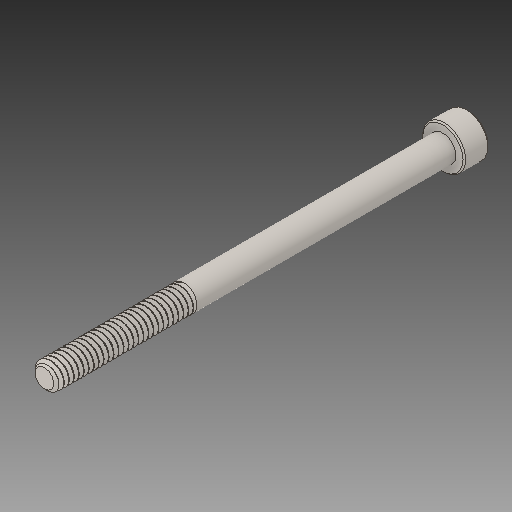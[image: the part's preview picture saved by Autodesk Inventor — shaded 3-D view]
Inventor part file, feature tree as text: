
AUTODESK INVENTOR PART (.ipt)
format: ipt  version: 2017 (Build 210142000, 142)  size: 690,688 bytes
history: native  units: in
note: dims shown in document units (in); Inventor stores cm internally (conversion verified against a paired STEP export)
features: chamfer x1
ambient origin geometry x8: Origin, YZ Plane, XZ Plane, XY Plane, X Axis, Y Axis, Z Axis, Center Point
bodies: Solid1 (feature_tree)
feature tree (1):
  chamfer  "Chamfer2"  [1 undecoded]
note: 1 required parameter value undecoded (feature->parameter linkage not recoverable at this tier; creation-order binding heuristic only, values carry confidence <= 0.55)
